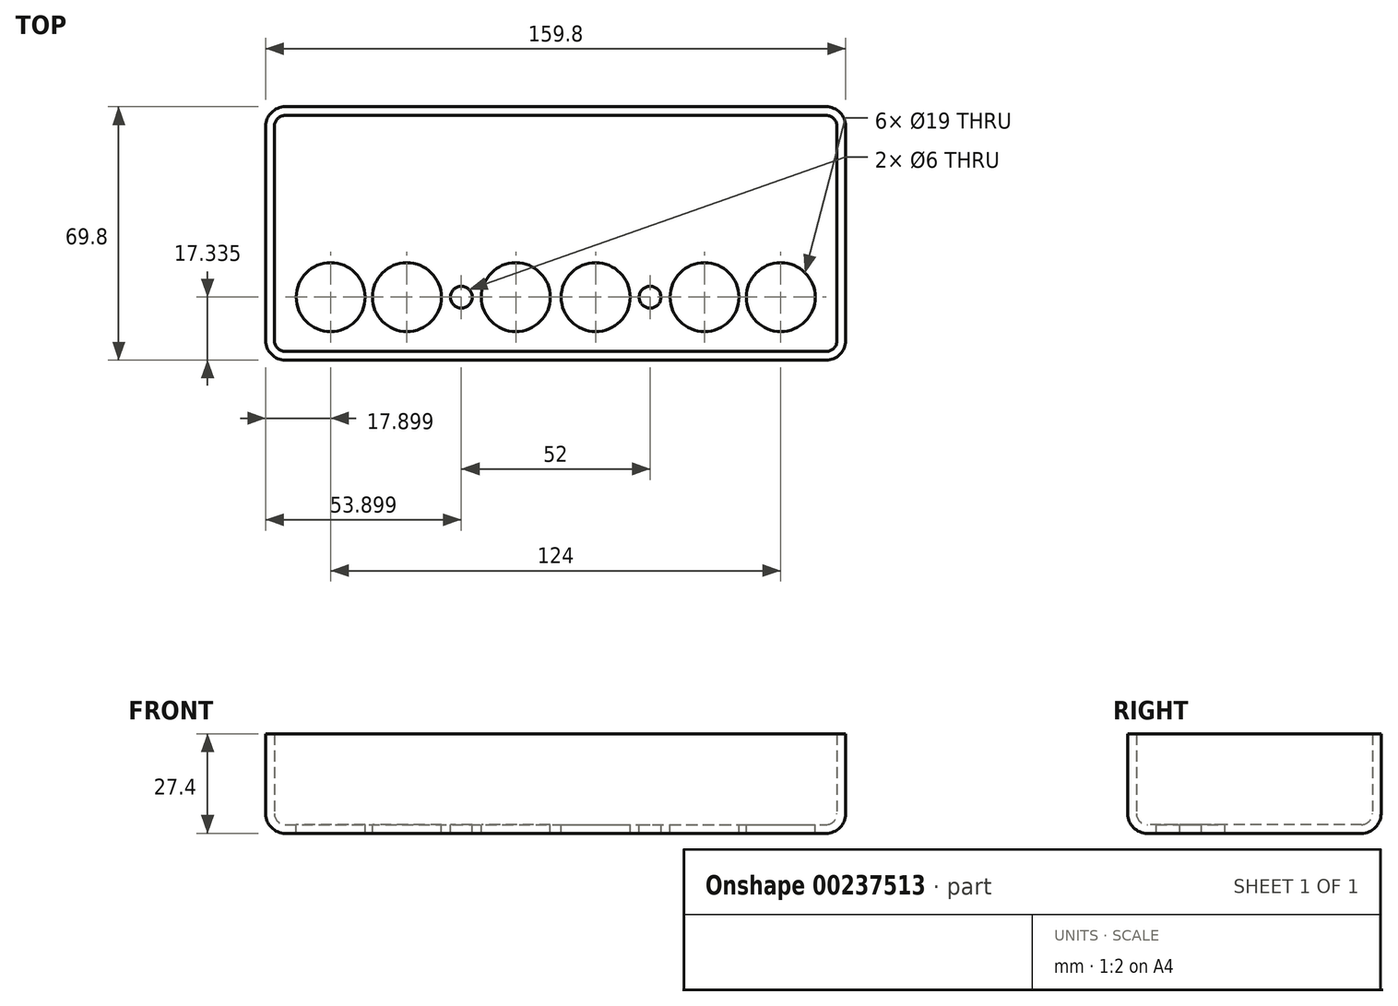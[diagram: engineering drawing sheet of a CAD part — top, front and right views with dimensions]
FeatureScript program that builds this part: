
annotation { "Feature Type Name" : "Feature", "Feature Type Description" : "" }
export const myFeature = defineFeature(function(context is Context, id is Id, definition is map)
    precondition{}
    {
        {
            var Q0;
            Q0=qCreatedBy(makeId("Top.planeOp"),FACE);
            var sketch = newSketch(context, id + "F0", { "sketchPlane" : qUnion([Q0])});
            skLineSegment(sketch, "E0.bottom", {"start": v(-81.37, 43.66) * mm, "end": v(-4.37, 43.66) * mm});
            skLineSegment(sketch, "E0.top", {"start": v(-81.37, -21.34) * mm, "end": v(-4.37, -21.34) * mm});
            skLineSegment(sketch, "E0.left", {"start": v(-81.37, 43.66) * mm, "end": v(-81.37, -21.34) * mm});
            skLineSegment(sketch, "E0.right", {"start": v(-4.37, 43.66) * mm, "end": v(-4.37, -21.34) * mm});
            skCircle(sketch, "E1", {"center": v(-14.87, -6.4) * mm, "radius": 9.5 * mm});
            skCircle(sketch, "E2", {"center": v(-44.87, -6.4) * mm, "radius": 9.5 * mm});
            skCircle(sketch, "E3", {"center": v(-65.87, -6.4) * mm, "radius": 9.5 * mm});
            skCircle(sketch, "E4", {"center": v(-29.87, -6.4) * mm, "radius": 3 * mm});
            skLineSegment(sketch, "E5", {"start": v(-3.87, 43.66) * mm, "end": v(-3.87, -21.34) * mm});
            skLineSegment(sketch, "E6", {"start": v(-4.37, 43.66) * mm, "end": v(-3.87, 43.66) * mm});
            skLineSegment(sketch, "E7", {"start": v(-4.37, -21.34) * mm, "end": v(-3.87, -21.34) * mm});
            skLineSegment(sketch, "E8.0", {"start": v(-83.67, 45.96) * mm, "end": v(-3.87, 45.96) * mm});
            skLineSegment(sketch, "E8.1", {"start": v(-83.67, 45.96) * mm, "end": v(-83.67, -23.64) * mm});
            skLineSegment(sketch, "E8.2", {"start": v(-83.67, -23.64) * mm, "end": v(-3.87, -23.64) * mm});
            skLineSegment(sketch, "E9", {"start": v(-3.87, 43.66) * mm, "end": v(-3.87, 45.96) * mm});
            skLineSegment(sketch, "E10", {"start": v(-3.87, -21.34) * mm, "end": v(-3.87, -23.64) * mm});
            skSolve(sketch);
        }
        {
            var Q0;
            Q0=makeQuery(id+"F0.imprint","IMPRINT",FACE,{"disambiguationData":[TD([[makeQuery(id+"F0.imprint","IMPRINT",EDGE,{"derivedFrom":sQuery(id+"F0.wireOp",EDGE,"E0.bottom")}),-1.0]])]});
            var Q1;
            Q1=makeQuery(id+"F0.imprint","IMPRINT",FACE,{"disambiguationData":[TD([[makeQuery(id+"F0.imprint","IMPRINT",EDGE,{"derivedFrom":sQuery(id+"F0.wireOp",EDGE,"E3")}),1.0]])]});
            var Q2;
            Q2=makeQuery(id+"F0.imprint","IMPRINT",FACE,{"disambiguationData":[TD([[makeQuery(id+"F0.imprint","IMPRINT",EDGE,{"derivedFrom":sQuery(id+"F0.wireOp",EDGE,"E2")}),1.0]])]});
            var Q3;
            Q3=makeQuery(id+"F0.imprint","IMPRINT",FACE,{"disambiguationData":[TD([[makeQuery(id+"F0.imprint","IMPRINT",EDGE,{"derivedFrom":sQuery(id+"F0.wireOp",EDGE,"E4")}),1.0]])]});
            var Q4;
            Q4=makeQuery(id+"F0.imprint","IMPRINT",FACE,{"disambiguationData":[TD([[makeQuery(id+"F0.imprint","IMPRINT",EDGE,{"derivedFrom":sQuery(id+"F0.wireOp",EDGE,"E1")}),1.0]])]});
            var Q5;
            Q5=makeQuery(id+"F0.imprint","IMPRINT",FACE,{"disambiguationData":[TD([[makeQuery(id+"F0.imprint","IMPRINT",EDGE,{"derivedFrom":sQuery(id+"F0.wireOp",EDGE,"E0.right")}),1.0]])]});
            extrude(context, id + "F1", {"entities" : qUnion([Q0, Q1, Q2, Q3, Q4, Q5]), "depth" : 25 * mm, "offsetDistance" : 25 * mm});
        }
        {
            var Q0;
            Q0=makeQuery(id+"F1.opExtrude","SWEPT_EDGE",EDGE,{"disambiguationData":[OSD([sQuery(id+"F0.wireOp",EDGE,"E0.top"),sQuery(id+"F0.wireOp",EDGE,"E0.left")])]});
            var Q1;
            Q1=makeQuery(id+"F1.opExtrude","SWEPT_EDGE",EDGE,{"disambiguationData":[OSD([sQuery(id+"F0.wireOp",EDGE,"E0.bottom"),sQuery(id+"F0.wireOp",EDGE,"E0.left")])]});
            var Q2;
            Q2=makeQuery(id+"F1.opExtrude","CAP_EDGE",EDGE,{"disambiguationData":[OSD([sQuery(id+"F0.wireOp",EDGE,"E0.bottom"),sQuery(id+"F0.wireOp",EDGE,"E6")])],"isStart":true});
            var Q3;
            Q3=makeQuery(id+"F1.opExtrude","CAP_EDGE",EDGE,{"disambiguationData":[OSD([sQuery(id+"F0.wireOp",EDGE,"E0.left")])],"isStart":true});
            var Q4;
            Q4=makeQuery(id+"F1.opExtrude","CAP_EDGE",EDGE,{"disambiguationData":[OSD([sQuery(id+"F0.wireOp",EDGE,"E0.top"),sQuery(id+"F0.wireOp",EDGE,"E7")])],"isStart":true});
            fillet(context, id + "F2", {"entities" : qUnion([Q0, Q1, Q2, Q3, Q4]), "radius" : 3 * mm, "tangentPropagation" : true, "allowEdgeOverflow" : false});
        }
        {
            var Q0;
            Q0=makeQuery(id+"F1.opExtrude","CAP_FACE",FACE,{"disambiguationData":[OSD([sQuery(id+"F0.wireOp",EDGE,"E0.bottom"),sQuery(id+"F0.wireOp",EDGE,"E0.top"),sQuery(id+"F0.wireOp",EDGE,"E0.left"),sQuery(id+"F0.wireOp",EDGE,"E0.right")])],"isStart":false});
            shell(context, id + "F3", {"entities" : qUnion([Q0]), "thickness" : 2.4 * mm, "oppositeDirection" : true});
        }
        {
            var Q0;
            Q0=makeQuery(id+"F0.imprint","IMPRINT",FACE,{"disambiguationData":[TD([[makeQuery(id+"F0.imprint","IMPRINT",EDGE,{"derivedFrom":sQuery(id+"F0.wireOp",EDGE,"E1")}),1.0]])]});
            var Q1;
            Q1=makeQuery(id+"F0.imprint","IMPRINT",FACE,{"disambiguationData":[TD([[makeQuery(id+"F0.imprint","IMPRINT",EDGE,{"derivedFrom":sQuery(id+"F0.wireOp",EDGE,"E4")}),1.0]])]});
            var Q2;
            Q2=makeQuery(id+"F0.imprint","IMPRINT",FACE,{"disambiguationData":[TD([[makeQuery(id+"F0.imprint","IMPRINT",EDGE,{"derivedFrom":sQuery(id+"F0.wireOp",EDGE,"E2")}),1.0]])]});
            var Q3;
            Q3=makeQuery(id+"F0.imprint","IMPRINT",FACE,{"disambiguationData":[TD([[makeQuery(id+"F0.imprint","IMPRINT",EDGE,{"derivedFrom":sQuery(id+"F0.wireOp",EDGE,"E3")}),1.0]])]});
            extrude(context, id + "F4", {"entities" : qUnion([Q0, Q1, Q2, Q3]), "operationType" : NewBodyOperationType.REMOVE, "endBound" : BoundingType.UP_TO_NEXT, "oppositeDirection" : true, "depth" : 25 * mm, "offsetDistance" : 25 * mm});
        }
        {
            var Q0;
            Q0=makeQuery(id+"F1.opExtrude","CAP_FACE",FACE,{"disambiguationData":[OSD([sQuery(id+"F0.wireOp",EDGE,"E0.bottom"),sQuery(id+"F0.wireOp",EDGE,"E0.top"),sQuery(id+"F0.wireOp",EDGE,"E0.left"),sQuery(id+"F0.wireOp",EDGE,"E5"),sQuery(id+"F0.wireOp",EDGE,"E6"),sQuery(id+"F0.wireOp",EDGE,"E7")])],"isStart":false});
            var sketch = newSketch(context, id + "F5", { "sketchPlane" : qUnion([Q0])});
            skLineSegment(sketch, "E11.bottom", {"start": v(-1.47, 46.06) * mm, "end": v(-3.87, 46.06) * mm});
            skLineSegment(sketch, "E11.top", {"start": v(-1.47, -23.74) * mm, "end": v(-3.87, -23.74) * mm});
            skLineSegment(sketch, "E11.left", {"start": v(-1.47, 46.06) * mm, "end": v(-1.47, -23.74) * mm});
            skLineSegment(sketch, "E11.right", {"start": v(-3.87, 46.06) * mm, "end": v(-3.87, -23.74) * mm});
            skSolve(sketch);
        }
        {
            var Q0;
            Q0 = qSketchRegion(id + "F5", true);
            extrude(context, id + "F6", {"entities" : qUnion([Q0]), "operationType" : NewBodyOperationType.REMOVE, "endBound" : BoundingType.UP_TO_NEXT, "oppositeDirection" : true, "depth" : 25 * mm, "offsetDistance" : 25 * mm});
        }
        {
            var Q0;
            Q0=makeQuery(id+"F1.opExtrude","SWEPT_BODY",BODY,{"disambiguationData":[OSD([sQuery(id+"F0.wireOp",EDGE,"E0.bottom"),sQuery(id+"F0.wireOp",EDGE,"E0.top"),sQuery(id+"F0.wireOp",EDGE,"E0.left"),sQuery(id+"F0.wireOp",EDGE,"E5"),sQuery(id+"F0.wireOp",EDGE,"E6"),sQuery(id+"F0.wireOp",EDGE,"E7")])]});
            var Q1;
            Q1=makeQuery(id+"F6.boolean.opBoolean","COPY",FACE,{"derivedFrom":makeQuery(id+"F6.opExtrude","SWEPT_FACE",FACE,{"disambiguationData":[OSD([sQuery(id+"F5.wireOp",EDGE,"E11.right")])]})});
            mirror(context, id + "F7", {"operationType" : NewBodyOperationType.ADD, "entities" : qUnion([Q0]), "mirrorPlane" : qUnion([Q1])});
        }
    });
